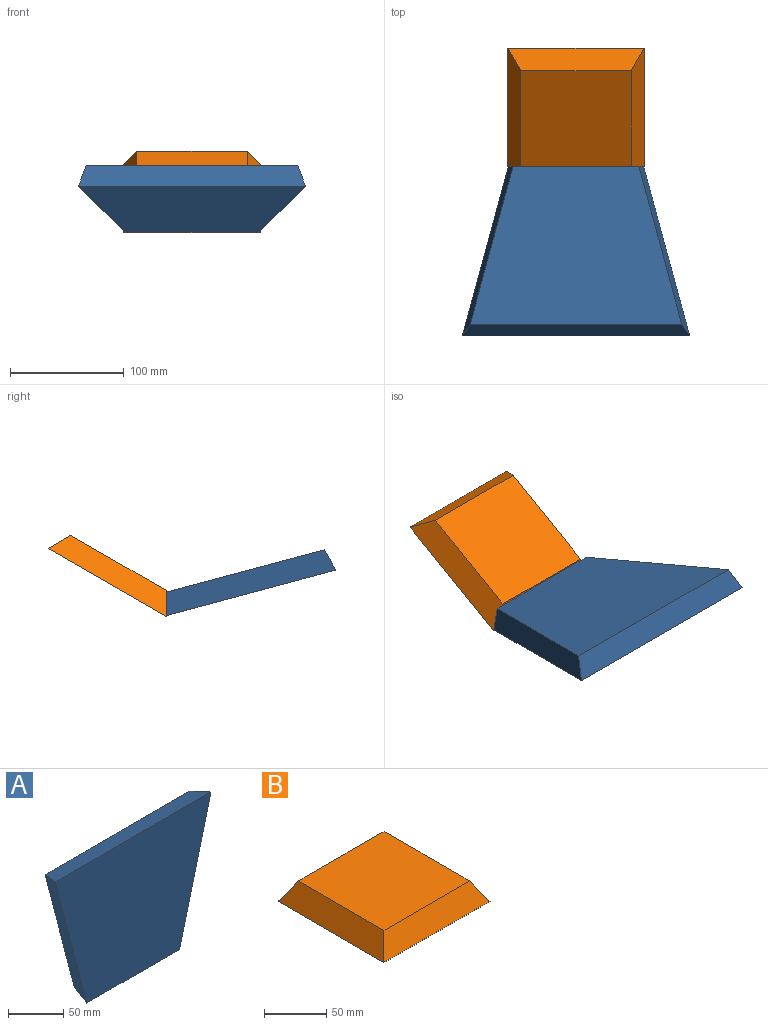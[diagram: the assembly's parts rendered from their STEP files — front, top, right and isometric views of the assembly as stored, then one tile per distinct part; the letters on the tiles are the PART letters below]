
ASSEMBLY  parts=2 mates=1
PART A: 6 faces, bbox 200x20x154.8 mm
  f0: plane 154.79x44.64mm, normal (-0.93,0.26,-0.24), area 3198.2mm2, adj f1,f3,f4,f5
  f1: plane 119x20mm, normal (0,0.26,-0.97), area 2378.3mm2, adj f0,f2,f4,f5
  f2: plane 154.79x44.64mm, normal (0.93,0.26,-0.24), area 3198.2mm2, adj f1,f3,f4,f5
  f3: plane 200x20mm, normal (0,0.26,0.97), area 3997.4mm2, adj f0,f2,f4,f5
  f4: plane 186.12x144.07mm, normal (0,1,0), area 21383.3mm2, adj f0,f1,f2,f3
  f5: plane 200x154.79mm, normal (0,-1,0), area 24688.9mm2, adj f0,f1,f2,f3
PART B: 6 faces, bbox 120x120x20 mm
  f0: plane 120x20mm, normal (0.87,0,0.5), area 2504.6mm2, adj f1,f3,f4,f5
  f1: plane 120x20mm, normal (0,0.87,0.5), area 2504.6mm2, adj f0,f2,f4,f5
  f2: plane 120x20mm, normal (-0.87,0,0.5), area 2504.6mm2, adj f1,f3,f4,f5
  f3: plane 120x20mm, normal (0,-0.87,0.5), area 2504.6mm2, adj f0,f2,f4,f5
  f4: plane 96.91x96.91mm, normal (0,0,1), area 9390.8mm2, adj f0,f1,f2,f3
  f5: plane 120x120mm, normal (0,0,-1), area 14400mm2, adj f0,f1,f2,f3
PLACE A rot(axis=(1,0,0),75deg) t=(23.31,-137.67,17.65)mm
PLACE B rot(axis=(1,0,0),30deg) t=(23.31,-10.95,26.71)mm
MATE fastened A.f1 <-> B.f3  axis (0,1,0) through (23.31,-62.91,7.85)mm
